# Revit family: ВВГФ-ВО
name_source: partatom
category: Арматура воздуховодов
units: mm (PartAtom-declared; Revit-internal decimal feet)

## family parameters
Всегда вертикально = Да
На основе рабочей плоскости = Нет
Общий = Нет
При загрузке вырезать с полостями = Нет
Размер круглого соединителя = Использовать диаметр
Тип детали = Присоединяется

## types (11) — shared parameters
00_20_Manufacturer = Вентс
00_20_Name = Гнучка вставка
Casing Material = Условный материал-отделка
Grid Material = Cover Grid Cross
L = 260 мм
Load Classification = HVAC
Maintenance zone material = <По категории>
l = 130 мм
l1 = 87 мм
t = 255 мм
zero-valued in all types: Отметка по умолчанию

## per-type parameters (varying)
| type | D1 | D2 | Dn | Dy | R1 | d | n | Вес |
| ВВГФ-ВО-400 | 450 мм | 490 мм | 410 мм | 400 мм | 225 мм | 8 мм | 12 | 4.76 кг |
| ВВГФ-ВО-450 | 500 мм | 540 мм | 460 мм | 450 мм | 250 мм | 8 мм | 12 | 5.34 кг |
| ВВГФ-ВО-500 | 560 мм | 600 мм | 510 мм | 500 мм | 280 мм | 12 мм | 12 | 6.12 кг |
| ВВГФ-ВО-560 | 620 мм | 660 мм | 570 мм | 560 мм | 310 мм | 12 мм | 12 | 6.83 кг |
| ВВГФ-ВО-630 | 690 мм | 730 мм | 640 мм | 630 мм | 345 мм | 12 мм | 12 | 7.66 кг |
| ВВГФ-ВО-710 | 770 мм | 810 мм | 720 мм | 710 мм | 385 мм | 12 мм | 16 | 8.6 кг |
| ВВГФ-ВО-800 | 860 мм | 900 мм | 810 мм | 800 мм | 430 мм | 12 мм | 16 | 9.67 кг |
| ВВГФ-ВО-900 | 970 мм | 1015 мм | 910 мм | 900 мм | 485 мм | 15 мм | 16 | 11.4 кг |
| ВВГФ-ВО-1000 | 1070 мм | 1115 мм | 1010 мм | 1000 мм | 535 мм | 15 мм | 16 | 12.64 кг |
| ВВГФ-ВО-1120 | 1190 мм | 1270 мм | 1130 мм | 1120 мм | 595 мм | 15 мм | 20 | 15.73 кг |
| ВВГФ-ВО-1250 | 1320 мм | 1400 мм | 1260 мм | 1250 мм | 660 мм | 15 мм | 20 | 17.52 кг |

note: column(s) folded — value = type name in every type: 00_20_Type
